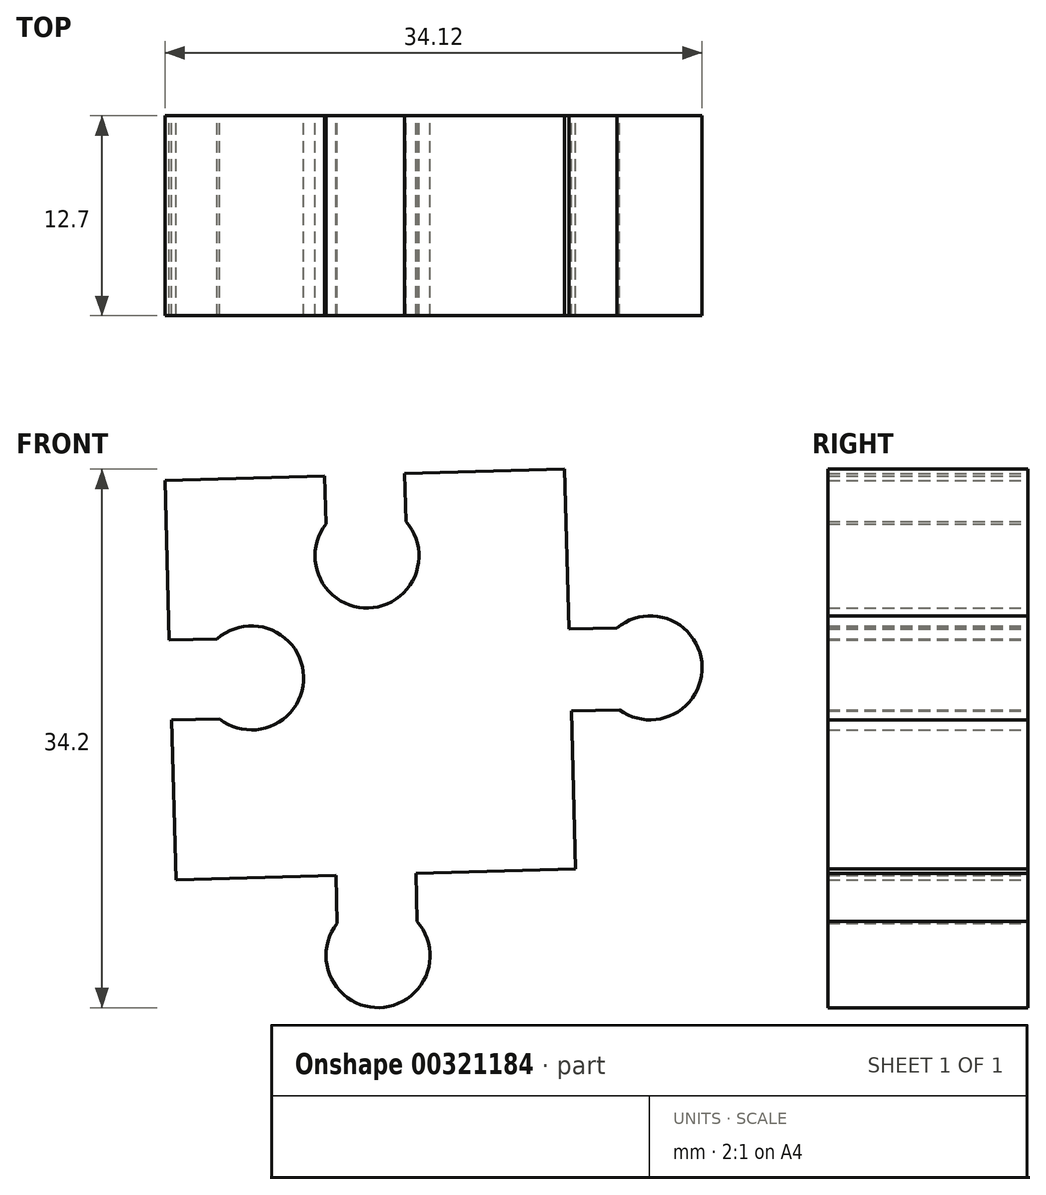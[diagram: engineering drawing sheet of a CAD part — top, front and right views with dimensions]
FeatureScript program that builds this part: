
annotation { "Feature Type Name" : "Feature", "Feature Type Description" : "" }
export const myFeature = defineFeature(function(context is Context, id is Id, definition is map)
    precondition{}
    {
        {
            var Q0;
            Q0=qCreatedBy(makeId("Front.planeOp"),FACE);
            var sketch = newSketch(context, id + "F0", { "sketchPlane" : qUnion([Q0])});
            skLineSegment(sketch, "E0", {"start": v(-21.02, 6.44) * mm, "end": v(-20.74, -3.72) * mm});
            skLineSegment(sketch, "E1", {"start": v(-21.02, 6.44) * mm, "end": v(-10.87, 6.72) * mm});
            skLineSegment(sketch, "E2", {"start": v(4.37, 7.14) * mm, "end": v(5.07, -18.25) * mm});
            skLineSegment(sketch, "E3", {"start": v(5.07, -18.25) * mm, "end": v(-20.32, -18.95) * mm});
            skLineSegment(sketch, "E4", {"start": v(-10.87, 6.72) * mm, "end": v(-10.78, 3.67) * mm});
            skLineSegment(sketch, "E5", {"start": v(-5.79, 6.86) * mm, "end": v(-5.7, 3.81) * mm});
            skArc(sketch, "E6", {"start": v(-10.78, 3.67) * mm, "mid": v(-8.1, -1.67) * mm, "end": v(-5.7, 3.81) * mm});
            skLineSegment(sketch, "E7.trimOffspring", {"start": v(-5.79, 6.86) * mm, "end": v(4.37, 7.14) * mm});
            skLineSegment(sketch, "E8", {"start": v(-10.17, -18.67) * mm, "end": v(-10.08, -21.72) * mm});
            skLineSegment(sketch, "E9", {"start": v(-5.09, -18.53) * mm, "end": v(-5, -21.58) * mm});
            skArc(sketch, "E10", {"start": v(-10.08, -21.72) * mm, "mid": v(-7.4, -27.06) * mm, "end": v(-5, -21.58) * mm});
            skLineSegment(sketch, "E11", {"start": v(-20.74, -3.72) * mm, "end": v(-17.7, -3.63) * mm});
            skLineSegment(sketch, "E12", {"start": v(-20.6, -8.8) * mm, "end": v(-17.56, -8.71) * mm});
            skArc(sketch, "E13", {"start": v(-17.56, -8.71) * mm, "mid": v(-12.22, -6.02) * mm, "end": v(-17.7, -3.63) * mm});
            skLineSegment(sketch, "E14.trimOffspring", {"start": v(-20.6, -8.8) * mm, "end": v(-20.32, -18.95) * mm});
            skLineSegment(sketch, "E15", {"start": v(4.65, -3.02) * mm, "end": v(7.7, -2.93) * mm});
            skLineSegment(sketch, "E16", {"start": v(4.8, -8.22) * mm, "end": v(7.84, -8.14) * mm});
            skArc(sketch, "E17", {"start": v(7.84, -8.14) * mm, "mid": v(13.1, -5.39) * mm, "end": v(7.7, -2.93) * mm});
            skSolve(sketch);
        }
        {
            var Q0;
            Q0 = qSketchRegion(id + "F0", true);
            extrude(context, id + "F1", {"entities" : qUnion([Q0]), "depth" : 12.7 * mm});
        }
    });
